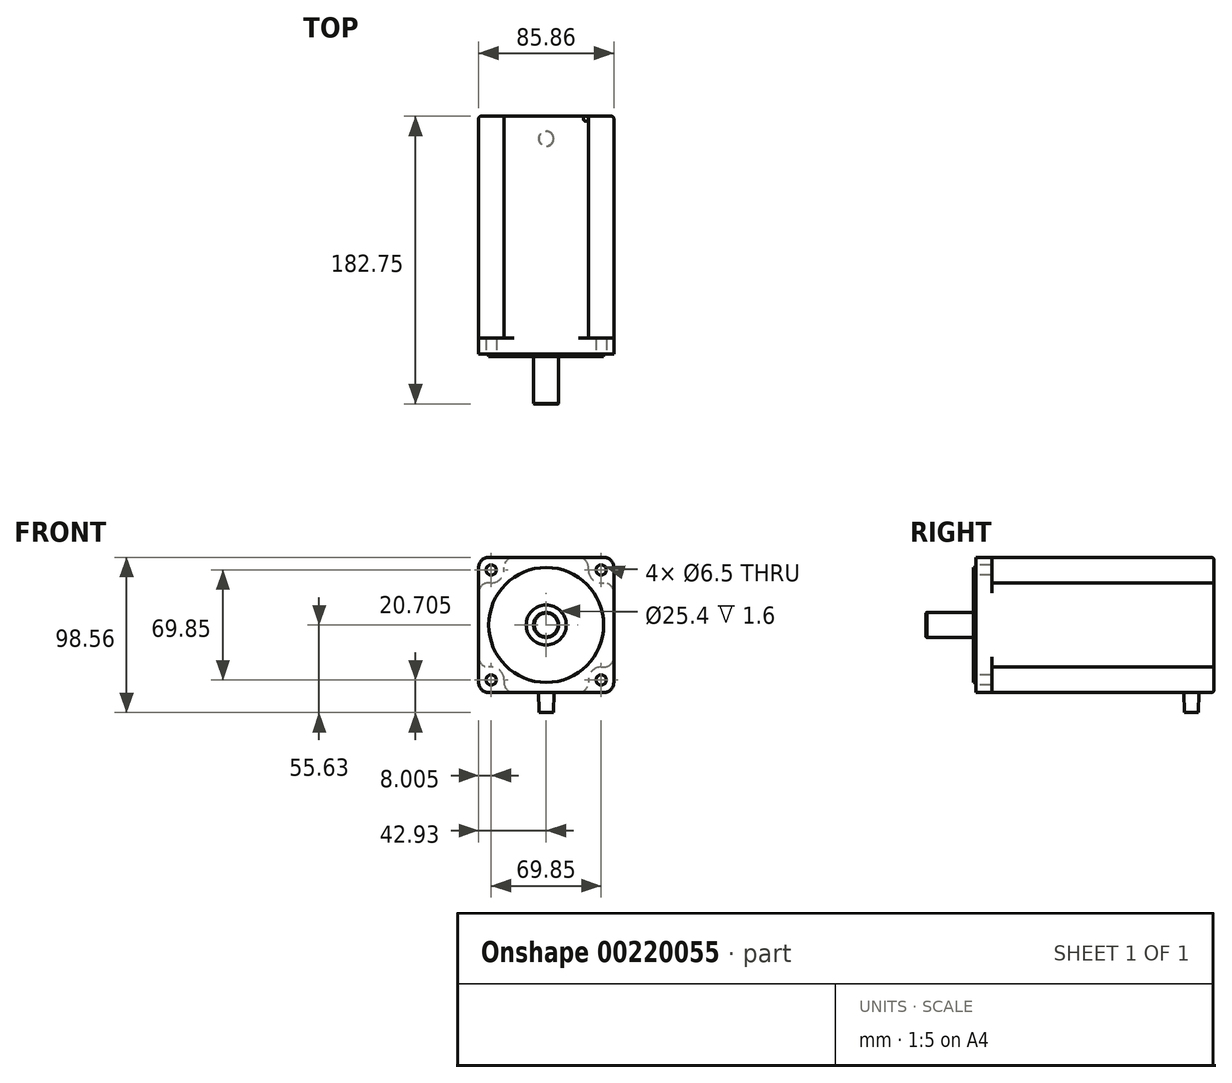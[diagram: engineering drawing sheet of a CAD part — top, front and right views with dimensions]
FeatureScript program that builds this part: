
annotation { "Feature Type Name" : "Feature", "Feature Type Description" : "" }
export const myFeature = defineFeature(function(context is Context, id is Id, definition is map)
    precondition{}
    {
        {
            var Q0;
            Q0=qCreatedBy(makeId("Front.planeOp"),FACE);
            var sketch = newSketch(context, id + "F0", { "sketchPlane" : qUnion([Q0])});
            skLineSegment(sketch, "E0.bottom", {"start": v(36.58, 42.93) * mm, "end": v(-36.58, 42.93) * mm});
            skLineSegment(sketch, "E0.top", {"start": v(36.58, -42.93) * mm, "end": v(-36.58, -42.93) * mm});
            skLineSegment(sketch, "E0.left", {"start": v(42.93, 36.58) * mm, "end": v(42.93, -36.58) * mm});
            skLineSegment(sketch, "E0.right", {"start": v(-42.93, 36.58) * mm, "end": v(-42.93, -36.58) * mm});
            skPoint(sketch, "E0.middle", {"position": v(0, 0) * mm});
            skLineSegment(sketch, "E1.bottom", {"start": v(34.93, 34.93) * mm, "end": v(-34.93, 34.93) * mm, "construction": true});
            skLineSegment(sketch, "E1.top", {"start": v(34.93, -34.93) * mm, "end": v(-34.93, -34.93) * mm, "construction": true});
            skLineSegment(sketch, "E1.left", {"start": v(34.93, 34.93) * mm, "end": v(34.93, -34.93) * mm, "construction": true});
            skLineSegment(sketch, "E1.right", {"start": v(-34.93, 34.93) * mm, "end": v(-34.93, -34.93) * mm, "construction": true});
            skCircle(sketch, "E2", {"center": v(-34.93, 34.93) * mm, "radius": 3.25 * mm});
            skCircle(sketch, "E3", {"center": v(34.93, 34.93) * mm, "radius": 3.25 * mm});
            skCircle(sketch, "E4", {"center": v(34.93, -34.93) * mm, "radius": 3.25 * mm});
            skCircle(sketch, "E5", {"center": v(-34.93, -34.93) * mm, "radius": 3.25 * mm});
            skPoint(sketch, "E6.visualSharp", {"position": v(42.93, 42.93) * mm});
            skArc(sketch, "E6.filletArc", {"start": v(42.93, 36.58) * mm, "mid": v(41.07, 41.07) * mm, "end": v(36.58, 42.93) * mm});
            skPoint(sketch, "E7.visualSharp", {"position": v(42.93, -42.93) * mm});
            skArc(sketch, "E7.filletArc", {"start": v(36.58, -42.93) * mm, "mid": v(41.07, -41.07) * mm, "end": v(42.93, -36.58) * mm});
            skPoint(sketch, "E8.visualSharp", {"position": v(-42.93, -42.93) * mm});
            skArc(sketch, "E8.filletArc", {"start": v(-42.93, -36.58) * mm, "mid": v(-41.07, -41.07) * mm, "end": v(-36.58, -42.93) * mm});
            skPoint(sketch, "E9.visualSharp", {"position": v(-42.93, 42.93) * mm});
            skArc(sketch, "E9.filletArc", {"start": v(-36.58, 42.93) * mm, "mid": v(-41.07, 41.07) * mm, "end": v(-42.93, 36.58) * mm});
            skSolve(sketch);
        }
        {
            var Q0;
            Q0 = qSketchRegion(id + "F0", true);
            extrude(context, id + "F1", {"entities" : qUnion([Q0]), "oppositeDirection" : true, "depth" : 10 * mm});
        }
        {
            var Q0;
            Q0=qCreatedBy(makeId("Front.planeOp"),FACE);
            var sketch = newSketch(context, id + "F2", { "sketchPlane" : qUnion([Q0])});
            skCircle(sketch, "E10", {"center": v(0, 0) * mm, "radius": 36.5 * mm});
            skSolve(sketch);
        }
        {
            var Q0;
            Q0 = qSketchRegion(id + "F2", true);
            extrude(context, id + "F3", {"entities" : qUnion([Q0]), "operationType" : NewBodyOperationType.ADD, "depth" : 1.6 * mm});
        }
        {
            var Q0;
            Q0=qCreatedBy(makeId("Front.planeOp"),FACE);
            var sketch = newSketch(context, id + "F4", { "sketchPlane" : qUnion([Q0])});
            skCircle(sketch, "E11", {"center": v(0, 0) * mm, "radius": 7.94 * mm});
            skSolve(sketch);
        }
        {
            var Q0;
            Q0 = qSketchRegion(id + "F4", true);
            extrude(context, id + "F5", {"entities" : qUnion([Q0]), "operationType" : NewBodyOperationType.ADD, "depth" : 31.75 * mm});
        }
        {
            var Q0;
            Q0=makeQuery(id+"F5.opExtrude","CAP_EDGE",EDGE,{"disambiguationData":[OSD([sQuery(id+"F4.wireOp",EDGE,"E11")])],"isStart":false});
            chamfer(context, id + "F6", {"entities" : qUnion([Q0]), "width" : 0.38 * mm, "tangentPropagation" : true});
        }
        {
            var Q0;
            Q0=makeQuery(id+"F3.opExtrude","CAP_FACE",FACE,{"disambiguationData":[OSD([sQuery(id+"F2.wireOp",EDGE,"E10")])],"isStart":false});
            var sketch = newSketch(context, id + "F7", { "sketchPlane" : qUnion([Q0])});
            skCircle(sketch, "E12.0", {"center": v(0, 0) * mm, "radius": 7.94 * mm});
            skCircle(sketch, "E13", {"center": v(0, 0) * mm, "radius": 12.7 * mm});
            skSolve(sketch);
        }
        {
            var Q0;
            Q0 = qSketchRegion(id + "F7", true);
            extrude(context, id + "F8", {"entities" : qUnion([Q0]), "operationType" : NewBodyOperationType.REMOVE, "oppositeDirection" : true, "depth" : 1.6 * mm});
        }
        {
            var Q0;
            Q0=makeQuery(id+"F1.opExtrude","CAP_FACE",FACE,{"disambiguationData":[OSD([sQuery(id+"F0.wireOp",EDGE,"E0.bottom"),sQuery(id+"F0.wireOp",EDGE,"E0.top"),sQuery(id+"F0.wireOp",EDGE,"E0.left"),sQuery(id+"F0.wireOp",EDGE,"E0.right"),sQuery(id+"F0.wireOp",EDGE,"E2"),sQuery(id+"F0.wireOp",EDGE,"E3"),sQuery(id+"F0.wireOp",EDGE,"E4"),sQuery(id+"F0.wireOp",EDGE,"E5"),sQuery(id+"F0.wireOp",EDGE,"E6.filletArc"),sQuery(id+"F0.wireOp",EDGE,"E7.filletArc"),sQuery(id+"F0.wireOp",EDGE,"E8.filletArc"),sQuery(id+"F0.wireOp",EDGE,"E9.filletArc")])],"isStart":false});
            var sketch = newSketch(context, id + "F9", { "sketchPlane" : qUnion([Q0])});
            skCircle(sketch, "E14.0", {"center": v(-34.93, 34.93) * mm, "radius": 3.25 * mm, "construction": true});
            skCircle(sketch, "E15.0", {"center": v(34.93, 34.93) * mm, "radius": 3.25 * mm, "construction": true});
            skCircle(sketch, "E16.0", {"center": v(34.93, -34.93) * mm, "radius": 3.25 * mm, "construction": true});
            skCircle(sketch, "E17.0", {"center": v(-34.93, -34.93) * mm, "radius": 3.25 * mm, "construction": true});
            skArc(sketch, "E18", {"start": v(-34.93, 26.76) * mm, "mid": v(-29.15, 29.15) * mm, "end": v(-26.76, 34.93) * mm});
            skArc(sketch, "E19", {"start": v(26.76, 34.93) * mm, "mid": v(29.15, 29.15) * mm, "end": v(34.93, 26.76) * mm});
            skArc(sketch, "E20", {"start": v(-26.76, -34.93) * mm, "mid": v(-29.15, -29.15) * mm, "end": v(-34.93, -26.76) * mm});
            skLineSegment(sketch, "E21", {"start": v(-34.93, 26.76) * mm, "end": v(-42.93, 26.76) * mm});
            skLineSegment(sketch, "E22", {"start": v(34.93, 26.76) * mm, "end": v(42.93, 26.76) * mm});
            skLineSegment(sketch, "E23", {"start": v(34.93, -26.76) * mm, "end": v(42.93, -26.76) * mm});
            skLineSegment(sketch, "E24", {"start": v(-26.76, 34.93) * mm, "end": v(-26.76, 42.93) * mm});
            skLineSegment(sketch, "E25", {"start": v(26.76, 34.93) * mm, "end": v(26.76, 42.93) * mm});
            skLineSegment(sketch, "E26", {"start": v(26.76, -34.93) * mm, "end": v(26.76, -42.93) * mm});
            skLineSegment(sketch, "E27", {"start": v(-26.76, -34.93) * mm, "end": v(-26.76, -42.93) * mm});
            skLineSegment(sketch, "E28", {"start": v(-34.93, -26.76) * mm, "end": v(-42.93, -26.76) * mm});
            skLineSegment(sketch, "E29.trimOffspring", {"start": v(-26.76, 42.93) * mm, "end": v(26.76, 42.93) * mm});
            skLineSegment(sketch, "E30.trimOffspring", {"start": v(-42.93, 26.76) * mm, "end": v(-42.93, -26.76) * mm});
            skLineSegment(sketch, "E31.trimOffspring", {"start": v(42.93, 26.76) * mm, "end": v(42.93, -26.76) * mm});
            skArc(sketch, "E32.trimOffspring", {"start": v(34.93, -26.76) * mm, "mid": v(29.15, -29.15) * mm, "end": v(26.76, -34.93) * mm});
            skLineSegment(sketch, "E33.trimOffspring", {"start": v(-26.76, -42.93) * mm, "end": v(26.76, -42.93) * mm});
            skPoint(sketch, "E34.0.start.orphan", {"position": v(-36.58, -42.93) * mm});
            skPoint(sketch, "E35.orphan", {"position": v(-42.93, -36.58) * mm});
            skPoint(sketch, "E36.0.start.orphan", {"position": v(-42.93, 36.58) * mm});
            skPoint(sketch, "E37.0.start.orphan", {"position": v(-36.58, 42.93) * mm});
            skPoint(sketch, "E38.trimOffspring.end.orphan", {"position": v(36.58, 42.93) * mm});
            skPoint(sketch, "E39.0.start.orphan", {"position": v(42.93, 36.58) * mm});
            skPoint(sketch, "E40.trimOffspring.end.orphan", {"position": v(42.93, -36.58) * mm});
            skPoint(sketch, "E41.trimOffspring.end.orphan", {"position": v(36.58, -42.93) * mm});
            skSolve(sketch);
        }
        {
            var Q0;
            Q0 = qSketchRegion(id + "F9", true);
            var Q1;
            Q1=sQuery(id+"F9.wireOp",EDGE,"E14.0");
            var Q2;
            Q2=sQuery(id+"F9.wireOp",EDGE,"E15.0");
            var Q3;
            Q3=sQuery(id+"F9.wireOp",EDGE,"E16.0");
            var Q4;
            Q4=sQuery(id+"F9.wireOp",EDGE,"E17.0");
            extrude(context, id + "F10", {"entities" : qUnion([Q0]), "operationType" : NewBodyOperationType.ADD, "surfaceEntities" : qUnion([Q1, Q2, Q3, Q4]), "depth" : 141 * mm});
        }
        {
            var Q0;
            Q0=makeQuery(id+"F10.opExtrude","SWEPT_EDGE",EDGE,{"disambiguationData":[OSD([sQuery(id+"F0.wireOp",EDGE,"E0.bottom"),sQuery(id+"F9.wireOp",EDGE,"E24"),sQuery(id+"F9.wireOp",EDGE,"E29.trimOffspring")])]});
            var Q1;
            Q1=makeQuery(id+"F10.opExtrude","SWEPT_EDGE",EDGE,{"disambiguationData":[OSD([sQuery(id+"F0.wireOp",EDGE,"E0.left"),sQuery(id+"F9.wireOp",EDGE,"E21"),sQuery(id+"F9.wireOp",EDGE,"E30.trimOffspring")])]});
            var Q2;
            Q2=makeQuery(id+"F10.opExtrude","SWEPT_EDGE",EDGE,{"disambiguationData":[OSD([sQuery(id+"F0.wireOp",EDGE,"E0.left"),sQuery(id+"F9.wireOp",EDGE,"E28"),sQuery(id+"F9.wireOp",EDGE,"E30.trimOffspring")])]});
            var Q3;
            Q3=makeQuery(id+"F10.opExtrude","SWEPT_EDGE",EDGE,{"disambiguationData":[OSD([sQuery(id+"F0.wireOp",EDGE,"E0.top"),sQuery(id+"F9.wireOp",EDGE,"E27"),sQuery(id+"F9.wireOp",EDGE,"E33.trimOffspring")])]});
            var Q4;
            Q4=makeQuery(id+"F10.opExtrude","SWEPT_EDGE",EDGE,{"disambiguationData":[OSD([sQuery(id+"F0.wireOp",EDGE,"E0.bottom"),sQuery(id+"F9.wireOp",EDGE,"E25"),sQuery(id+"F9.wireOp",EDGE,"E29.trimOffspring")])]});
            var Q5;
            Q5=makeQuery(id+"F10.opExtrude","SWEPT_EDGE",EDGE,{"disambiguationData":[OSD([sQuery(id+"F0.wireOp",EDGE,"E0.right"),sQuery(id+"F9.wireOp",EDGE,"E22"),sQuery(id+"F9.wireOp",EDGE,"E31.trimOffspring")])]});
            var Q6;
            Q6=makeQuery(id+"F10.opExtrude","SWEPT_EDGE",EDGE,{"disambiguationData":[OSD([sQuery(id+"F0.wireOp",EDGE,"E0.right"),sQuery(id+"F9.wireOp",EDGE,"E23"),sQuery(id+"F9.wireOp",EDGE,"E31.trimOffspring")])]});
            var Q7;
            Q7=makeQuery(id+"F10.opExtrude","SWEPT_EDGE",EDGE,{"disambiguationData":[OSD([sQuery(id+"F0.wireOp",EDGE,"E0.top"),sQuery(id+"F9.wireOp",EDGE,"E26"),sQuery(id+"F9.wireOp",EDGE,"E33.trimOffspring")])]});
            fillet(context, id + "F11", {"entities" : qUnion([Q0, Q1, Q2, Q3, Q4, Q5, Q6, Q7]), "radius" : 6.35 * mm, "tangentPropagation" : true, "allowEdgeOverflow" : false});
        }
        {
            var Q0;
            {var subQ0=sQuery(id+"F9.wireOp",EDGE,"E29.trimOffspring");var subQ1=sQuery(id+"F9.wireOp",EDGE,"E24");Q0=makeQuery(id+"F11.opFillet","BLEND_EDGE",EDGE,{"blendedFrom":[makeQuery(id+"F10.opExtrude","SWEPT_EDGE",EDGE,{"disambiguationData":[OSD([sQuery(id+"F0.wireOp",EDGE,"E0.bottom"),subQ1,subQ0])]}),makeQuery(id+"F10.opExtrude","CAP_FACE",FACE,{"disambiguationData":[OSD([sQuery(id+"F9.wireOp",EDGE,"E18"),sQuery(id+"F9.wireOp",EDGE,"E19"),sQuery(id+"F9.wireOp",EDGE,"E20"),sQuery(id+"F9.wireOp",EDGE,"E21"),sQuery(id+"F9.wireOp",EDGE,"E22"),sQuery(id+"F9.wireOp",EDGE,"E23"),subQ1,sQuery(id+"F9.wireOp",EDGE,"E25"),sQuery(id+"F9.wireOp",EDGE,"E26"),sQuery(id+"F9.wireOp",EDGE,"E27"),sQuery(id+"F9.wireOp",EDGE,"E28"),subQ0,sQuery(id+"F9.wireOp",EDGE,"E30.trimOffspring"),sQuery(id+"F9.wireOp",EDGE,"E31.trimOffspring"),sQuery(id+"F9.wireOp",EDGE,"E32.trimOffspring"),sQuery(id+"F9.wireOp",EDGE,"E33.trimOffspring")])],"isStart":false})],"blendedInto":[makeQuery(id+"F10.opExtrude","CAP_FACE",FACE,{"disambiguationData":[OSD([sQuery(id+"F9.wireOp",EDGE,"E18"),sQuery(id+"F9.wireOp",EDGE,"E19"),sQuery(id+"F9.wireOp",EDGE,"E20"),sQuery(id+"F9.wireOp",EDGE,"E21"),sQuery(id+"F9.wireOp",EDGE,"E22"),sQuery(id+"F9.wireOp",EDGE,"E23"),subQ1,sQuery(id+"F9.wireOp",EDGE,"E25"),sQuery(id+"F9.wireOp",EDGE,"E26"),sQuery(id+"F9.wireOp",EDGE,"E27"),sQuery(id+"F9.wireOp",EDGE,"E28"),subQ0,sQuery(id+"F9.wireOp",EDGE,"E30.trimOffspring"),sQuery(id+"F9.wireOp",EDGE,"E31.trimOffspring"),sQuery(id+"F9.wireOp",EDGE,"E32.trimOffspring"),sQuery(id+"F9.wireOp",EDGE,"E33.trimOffspring")])],"isStart":false})]});}
            fillet(context, id + "F12", {"entities" : qUnion([Q0]), "radius" : 1.6 * mm, "tangentPropagation" : true, "allowEdgeOverflow" : false});
        }
        {
            var Q0;
            Q0=makeQuery(id+"F10.boolean.opBoolean","MERGE",FACE,{"derivedFrom":[makeQuery(id+"F1.opExtrude","SWEPT_FACE",FACE,{"disambiguationData":[OSD([sQuery(id+"F0.wireOp",EDGE,"E0.top")])]}),makeQuery(id+"F10.opExtrude","SWEPT_FACE",FACE,{"disambiguationData":[OSD([sQuery(id+"F9.wireOp",EDGE,"E33.trimOffspring")])]})]});
            var sketch = newSketch(context, id + "F13", { "sketchPlane" : qUnion([Q0])});
            skLineSegment(sketch, "E42", {"start": v(0, 0) * mm, "end": v(0, -149.4) * mm, "construction": true});
            skPoint(sketch, "E43.endSnap0", {"position": v(0, -149.4) * mm});
            skCircle(sketch, "E44", {"center": v(0, -136.7) * mm, "radius": 4.83 * mm});
            skSolve(sketch);
        }
        {
            var Q0;
            Q0 = qSketchRegion(id + "F13", true);
            extrude(context, id + "F14", {"entities" : qUnion([Q0]), "operationType" : NewBodyOperationType.ADD, "depth" : 12.7 * mm, "hasDraft" : true, "draftAngle" : 1 * degree, "draftPullDirection" : true});
        }
    });
